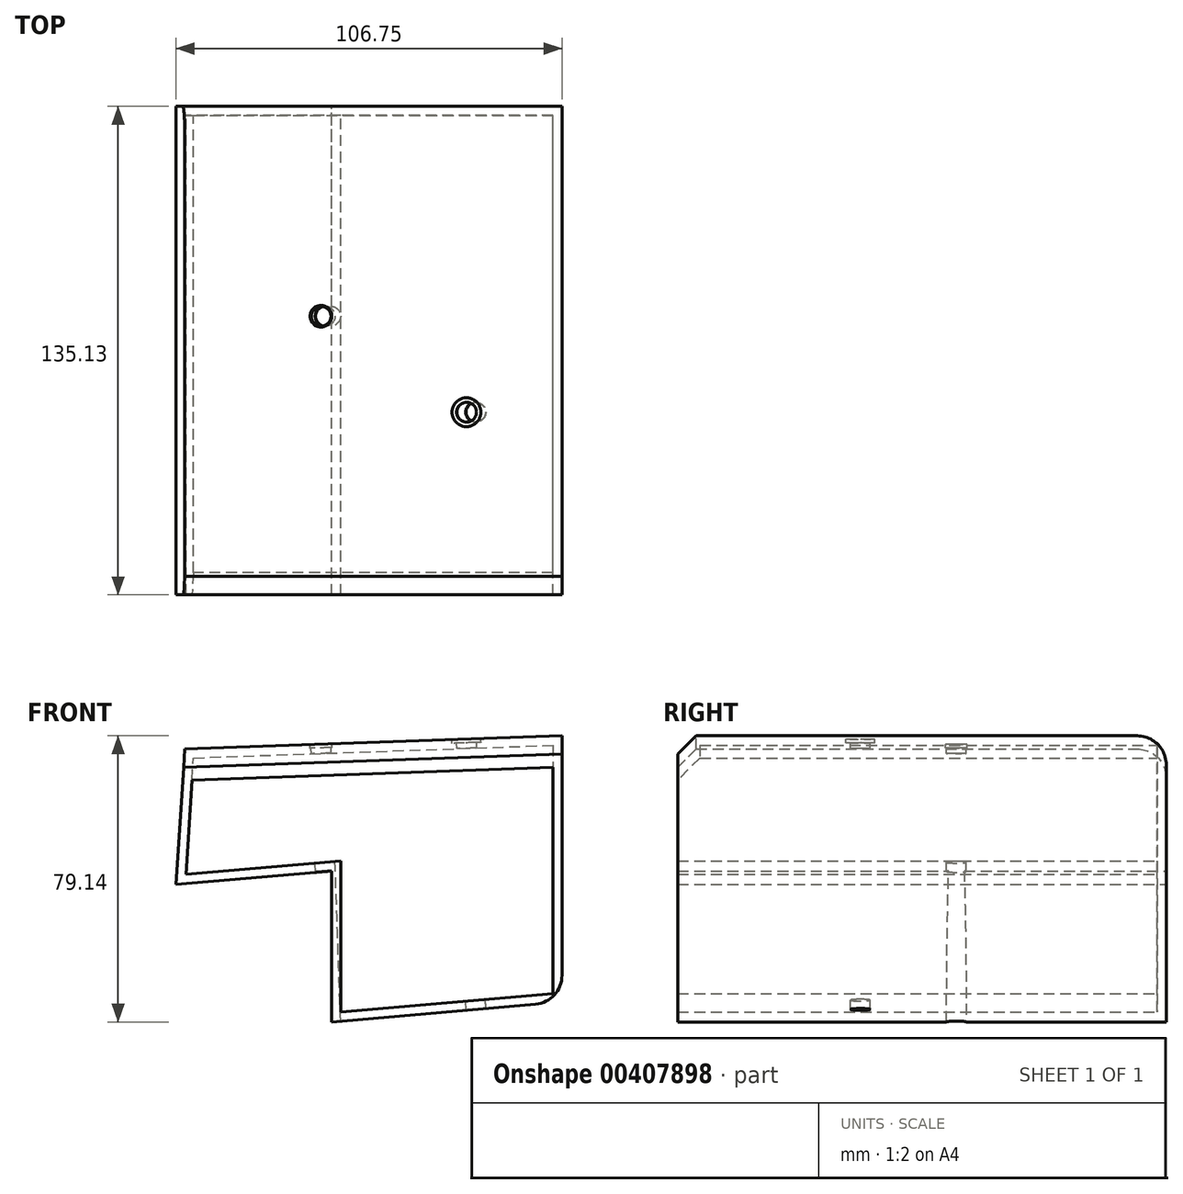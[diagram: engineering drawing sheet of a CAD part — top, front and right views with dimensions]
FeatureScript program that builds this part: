
annotation { "Feature Type Name" : "Feature", "Feature Type Description" : "" }
export const myFeature = defineFeature(function(context is Context, id is Id, definition is map)
    precondition{}
    {
        {
            var Q0;
            Q0=qCreatedBy(makeId("Front.planeOp"),FACE);
            var sketch = newSketch(context, id + "F0", { "sketchPlane" : qUnion([Q0])});
            skLineSegment(sketch, "E0.bottom", {"start": v(-28.84, 27.42) * mm, "end": v(42.7, 27.42) * mm});
            skLineSegment(sketch, "E0.top", {"start": v(-28.84, -36.75) * mm, "end": v(42.7, -36.75) * mm});
            skLineSegment(sketch, "E0.left", {"start": v(-28.84, 27.42) * mm, "end": v(-28.84, -36.75) * mm});
            skLineSegment(sketch, "E0.right", {"start": v(42.7, 27.42) * mm, "end": v(42.7, -36.75) * mm});
            skSolve(sketch);
        }
        {
            var Q0;
            Q0=makeQuery(id+"F0.imprint","IMPRINT",FACE,{"disambiguationData":[TD([[makeQuery(id+"F0.imprint","IMPRINT",EDGE,{"derivedFrom":sQuery(id+"F0.wireOp",EDGE,"E0.bottom")}),-1.0]])]});
            extrude(context, id + "F1", {"entities" : qUnion([Q0]), "depth" : 89.92 * mm});
        }
        {
            var Q0;
            Q0=makeQuery(id+"F1.opExtrude","SWEPT_EDGE",EDGE,{"disambiguationData":[OSD([sQuery(id+"F0.wireOp",EDGE,"E0.bottom"),sQuery(id+"F0.wireOp",EDGE,"E0.right")])]});
            chamfer(context, id + "F2", {"entities" : qUnion([Q0]), "chamferType" : ChamferType.TWO_OFFSETS, "width1" : 5.08 * mm, "oppositeDirection" : false, "width2" : 25.4 * mm, "tangentPropagation" : true});
        }
        {
            var Q0;
            Q0=makeQuery(id+"F1.opExtrude","SWEPT_BODY",BODY,{"disambiguationData":[OSD([sQuery(id+"F0.wireOp",EDGE,"E0.bottom"),sQuery(id+"F0.wireOp",EDGE,"E0.top"),sQuery(id+"F0.wireOp",EDGE,"E0.left"),sQuery(id+"F0.wireOp",EDGE,"E0.right")])]});
            deleteBodies(context, id + "F3", {"entities" : qUnion([Q0])});
        }
        {
            var Q0;
            Q0=qCreatedBy(makeId("Front.planeOp"),FACE);
            var sketch = newSketch(context, id + "F4", { "sketchPlane" : qUnion([Q0])});
            skLineSegment(sketch, "E1", {"start": v(-64.01, 33.71) * mm, "end": v(40.33, 37.37) * mm});
            skLineSegment(sketch, "E2", {"start": v(40.33, 37.37) * mm, "end": v(40.33, -36.21) * mm});
            skLineSegment(sketch, "E3", {"start": v(40.33, -36.21) * mm, "end": v(-23.42, -41.77) * mm});
            skLineSegment(sketch, "E4", {"start": v(-23.42, -41.77) * mm, "end": v(-23.42, 0) * mm});
            skLineSegment(sketch, "E5", {"start": v(-23.42, 0) * mm, "end": v(-66.42, -3.66) * mm});
            skLineSegment(sketch, "E6", {"start": v(-66.42, -3.66) * mm, "end": v(-64.01, 33.71) * mm});
            skSolve(sketch);
        }
        {
            var Q0;
            Q0=makeQuery(id+"F4.imprint","IMPRINT",FACE,{"disambiguationData":[TD([[makeQuery(id+"F4.imprint","IMPRINT",EDGE,{"derivedFrom":sQuery(id+"F4.wireOp",EDGE,"E1")}),-1.0]])]});
            extrude(context, id + "F5", {"entities" : qUnion([Q0]), "depth" : 135.13 * mm});
        }
        {
            var Q0;
            Q0=makeQuery(id+"F5.opExtrude","CAP_EDGE",EDGE,{"disambiguationData":[OSD([sQuery(id+"F4.wireOp",EDGE,"E1")])],"isStart":false});
            chamfer(context, id + "F6", {"entities" : qUnion([Q0]), "width" : 5.08 * mm, "tangentPropagation" : true});
        }
        {
            var Q0;
            Q0=makeQuery(id+"F5.opExtrude","CAP_FACE",FACE,{"disambiguationData":[OSD([sQuery(id+"F4.wireOp",EDGE,"E1"),sQuery(id+"F4.wireOp",EDGE,"E2"),sQuery(id+"F4.wireOp",EDGE,"E3"),sQuery(id+"F4.wireOp",EDGE,"E4"),sQuery(id+"F4.wireOp",EDGE,"E5"),sQuery(id+"F4.wireOp",EDGE,"E6")])],"isStart":false});
            shell(context, id + "F7", {"entities" : qUnion([Q0]), "thickness" : 2.54 * mm});
        }
        {
            var Q0;
            Q0=makeQuery(id+"F5.opExtrude","SWEPT_FACE",FACE,{"disambiguationData":[OSD([sQuery(id+"F4.wireOp",EDGE,"E1")])]});
            var sketch = newSketch(context, id + "F8", { "sketchPlane" : qUnion([Q0])});
            skPoint(sketch, "E7", {"position": v(-7.55, -63.5) * mm});
            skPoint(sketch, "E8", {"position": v(-25.1, -58.04) * mm});
            skPoint(sketch, "E9", {"position": v(-3.9, -101.67) * mm});
            skPoint(sketch, "E10", {"position": v(15.16, -84.6) * mm});
            skPoint(sketch, "E11", {"position": v(-33.02, -99.98) * mm});
            skSolve(sketch);
        }
        {
            var Q0;
            Q0=sQuery(id+"F8.wireOp",VERTEX,"E8");
            var Q1;
            Q1=makeQuery(id+"F5.opExtrude","SWEPT_BODY",BODY,{"disambiguationData":[OSD([sQuery(id+"F4.wireOp",EDGE,"E1"),sQuery(id+"F4.wireOp",EDGE,"E2"),sQuery(id+"F4.wireOp",EDGE,"E3"),sQuery(id+"F4.wireOp",EDGE,"E4"),sQuery(id+"F4.wireOp",EDGE,"E5"),sQuery(id+"F4.wireOp",EDGE,"E6")])]});
            hole(context, id + "F9", {"style" : HoleStyle.C_BORE, "endStyle" : HoleEndStyle.THROUGH, "holeDiameter" : 5.5 * mm, "cBoreDiameter" : 6 * mm, "cBoreDepth" : 1 * mm, "isTappedThrough" : true, "tappedDepth" : 12 * mm, "tapClearance" : 3, "startFromSketch" : true, "locations" : qUnion([Q0]), "scope" : qUnion([Q1])});
        }
        {
            var Q0;
            Q0=sQuery(id+"F8.wireOp",VERTEX,"E10");
            var Q1;
            Q1=makeQuery(id+"F5.opExtrude","SWEPT_BODY",BODY,{"disambiguationData":[OSD([sQuery(id+"F4.wireOp",EDGE,"E1"),sQuery(id+"F4.wireOp",EDGE,"E2"),sQuery(id+"F4.wireOp",EDGE,"E3"),sQuery(id+"F4.wireOp",EDGE,"E4"),sQuery(id+"F4.wireOp",EDGE,"E5"),sQuery(id+"F4.wireOp",EDGE,"E6")])]});
            hole(context, id + "F10", {"style" : HoleStyle.C_BORE, "endStyle" : HoleEndStyle.THROUGH, "holeDiameter" : 5.5 * mm, "cBoreDiameter" : 8 * mm, "cBoreDepth" : 1 * mm, "isTappedThrough" : true, "tappedDepth" : 12 * mm, "tapClearance" : 3, "startFromSketch" : true, "locations" : qUnion([Q0]), "scope" : qUnion([Q1])});
        }
        {
            var Q0;
            Q0=makeQuery(id+"F5.opExtrude","CAP_EDGE",EDGE,{"disambiguationData":[OSD([sQuery(id+"F4.wireOp",EDGE,"E1")])],"isStart":true});
            fillet(context, id + "F11", {"entities" : qUnion([Q0]), "radius" : 8 * mm, "tangentPropagation" : true, "allowEdgeOverflow" : false});
        }
        {
            var Q0;
            Q0=makeQuery(id+"F5.opExtrude","SWEPT_EDGE",EDGE,{"disambiguationData":[OSD([sQuery(id+"F4.wireOp",EDGE,"E2"),sQuery(id+"F4.wireOp",EDGE,"E3")])]});
            fillet(context, id + "F12", {"entities" : qUnion([Q0]), "radius" : 8 * mm, "tangentPropagation" : true, "allowEdgeOverflow" : false});
        }
    });
